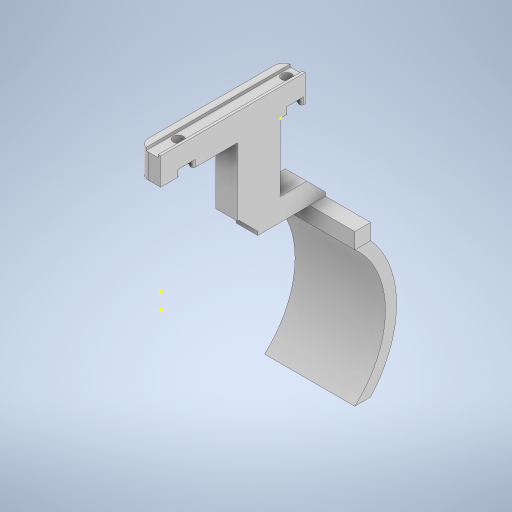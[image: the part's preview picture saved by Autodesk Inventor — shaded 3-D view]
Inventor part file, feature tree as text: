
AUTODESK INVENTOR PART (.ipt)
format: ipt  version: 2024 (Build 280153000, 153)  size: 395,264 bytes
history: native  units: in
note: dims shown in document units (in); Inventor stores cm internally (conversion verified against a paired STEP export)
features: sketch x13, extrude x8, projected_geometry x4, fillet x2, chamfer x2, sweep x1
ambient origin geometry x8: Origin, YZ Plane, XZ Plane, XY Plane, X Axis, Y Axis, Z Axis, Center Point
bodies: Solid1 (feature_tree), Solid4 (feature_tree)
feature tree (30):
  extrude  "Extrusion1"  Depth=2.5197in
  extrude  "Extrusion2"  Depth=1.8898in
  extrude  "Extrusion3"  Depth=0.4724in TaperAngle=0.0deg
  fillet  "Fillet1"  Radius=0.0433in
  fillet  "Fillet2"  Radius=0.2126in
  extrude  "Extrusion19"  Depth=0.4724in TaperAngle=0.0deg
  extrude  "Extrusion21"  Depth=0.1181in TaperAngle=0.0deg
  sketch  "Sketch41"  dims[d17=0.1772in d18=0.0394in]
  extrude  "Extrusion22"  Depth=0.0394in
  chamfer  "Chamfer4"  Distance=1.1811in
  chamfer  "Chamfer5"  Distance=0.3937in
  sketch  "Sketch60"  dims[d76=0.4724in]
  sketch  "Sketch61"  dims[d107=0.102in]
  sweep  "Sweep6"
  extrude  "Extrusion25"  Depth=1.5748in
  extrude  "Extrusion26"  Depth=0.2756in TaperAngle=0.0deg
  sketch  "Sketch1"  dims[d1=0.374in d2=2.5197in]
  sketch  "Sketch2"  dims[d3=0.1772in d4=1.8898in]
  sketch  "Sketch3"  dims[d6=0.1457in d7=0.4724in d8=0.0in d9=0.0433in d10=0.2126in]
  projected_geometry  "Projected Loop2"
  projected_geometry  "Projected Loop3"
  projected_geometry  "Projected Loop4"
  projected_geometry  "Projected Loop5"
  sketch  "Sketch28"  dims[d11=0.0472in d12=0.4724in d13=0.0in]
  sketch  "Sketch40"  dims[d14=0.2953in d15=0.1181in d16=0.0in]
  sketch  "Sketch42"  dims[d19=0.1575in]
  sketch  "Sketch62"  dims[d108=0.748in d109=1.1811in d110=0.0in]
  sketch  "Sketch63"  dims[d130=0.7874in]
  sketch  "Sketch64"  dims[d131=1.1811in d132=0.3937in d133=0.0in]
  sketch  "Sketch65"  dims[d134=0.7874in d135=0.2756in d137=1.5748in d138=0.2756in d139=0.0in d156=0.3287in d157=0.0787in d158=45.0deg d159=0.3287in d160=0.0787in d161=45.0deg d166=2.3622in d167=1.5748in d168=0.0in d169=0.0in d170=3.6688in d171=0.0in d172=0.3937in d173=0.5374in d174=0.0in d42=0.0197in d43=0.0344in d44=0.0197in d45=0.0344in d46=0.0in d47=0.0in d48=0.0in d49=0.0in d50=0.0in d51=0.0in d52=0.0in d53=0.0in d55=0.0197in d56=0.0344in d57=0.0197in d58=0.0344in d60=0.0197in d61=0.0344in d62=0.0197in d63=0.0344in d72=0.0197in d73=0.0344in d74=0.0197in d75=0.0344in d140=0.0197in d141=0.0344in d175=0.0197in d176=0.0344in]
